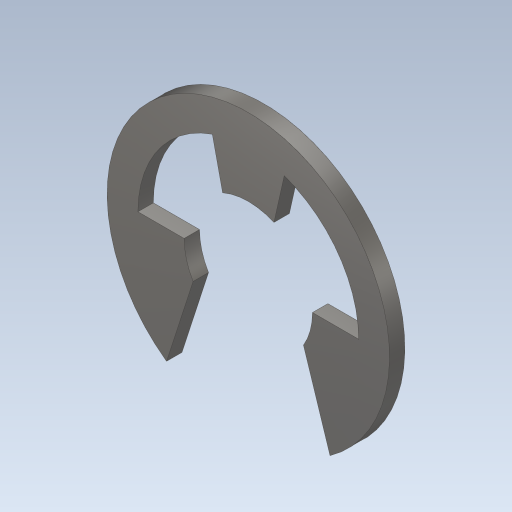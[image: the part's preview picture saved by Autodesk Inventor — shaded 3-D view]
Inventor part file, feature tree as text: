
AUTODESK INVENTOR PART (.ipt)
format: ipt  version: 2024 (Build 280153000, 153)  size: 141,312 bytes
history: native  units: mm
features: other x14, extrude x1, sketch x1
ambient origin geometry x8: Origin, YZ Plane, XZ Plane, XY Plane, X Axis, Y Axis, Z Axis, Center Point
bodies: Solid1 (feature_tree)
feature tree (16):
  extrude  "Extrusion1"  TaperAngle=0.0deg  [1 undecoded]
  other  "COMBINATION_MODULE_XY"
  other  "COMBINATION_MODULE_YZ"
  other  "COMBINATION_MODULE_ZX"
  other  "COMBINATION_MODULE_X"
  other  "COMBINATION_MODULE_Y"
  other  "COMBINATION_MODULE_Z"
  other  "COMBINATION_MODULE_Center"
  other  "ring_to_screw_XY"
  other  "ring_to_screw_YZ"
  other  "ring_to_screw_ZX"
  other  "ring_to_screw_X"
  other  "ring_to_screw_Y"
  other  "ring_to_screw_Z"
  other  "ring_to_screw_Center"
  sketch  "Sketch_1"  dims[d0=0.6mm d1=0.0mm d2=0.0mm]
note: 1 required parameter value undecoded (feature->parameter linkage not recoverable at this tier; creation-order binding heuristic only, values carry confidence <= 0.55)
